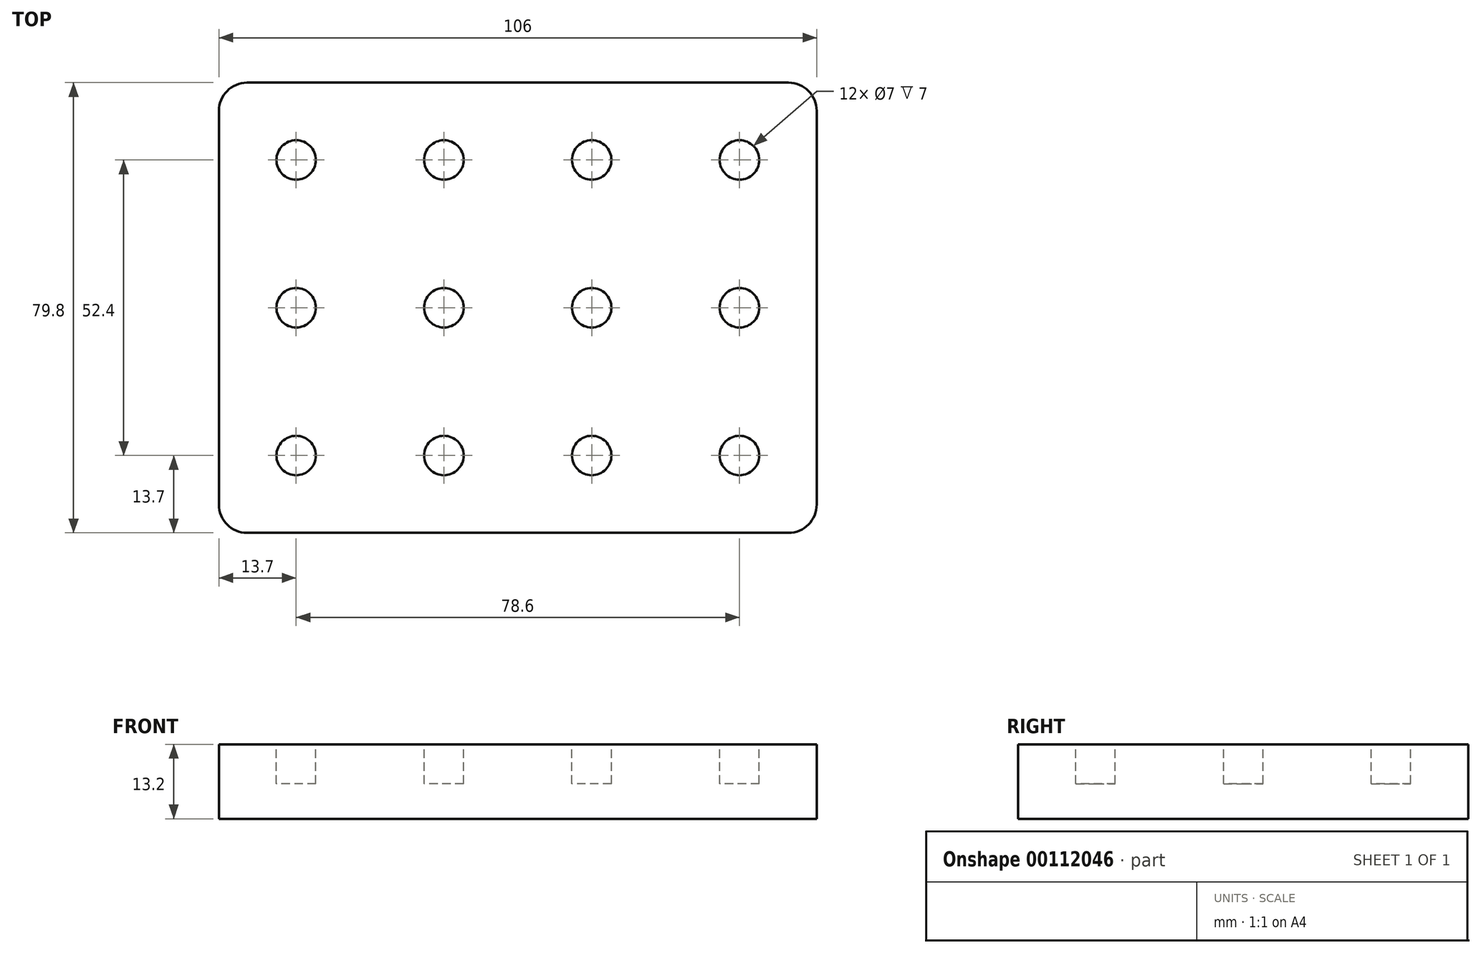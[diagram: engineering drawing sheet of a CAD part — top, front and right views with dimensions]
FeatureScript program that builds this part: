
annotation { "Feature Type Name" : "Feature", "Feature Type Description" : "" }
export const myFeature = defineFeature(function(context is Context, id is Id, definition is map)
    precondition{}
    {
        {
            var Q0;
            Q0=qCreatedBy(makeId("Top.planeOp"),FACE);
            var sketch = newSketch(context, id + "F0", { "sketchPlane" : qUnion([Q0])});
            skLineSegment(sketch, "E0.bottom", {"start": v(48, -39.9) * mm, "end": v(-48, -39.9) * mm});
            skLineSegment(sketch, "E0.top", {"start": v(48, 39.9) * mm, "end": v(-48, 39.9) * mm});
            skLineSegment(sketch, "E0.left", {"start": v(53, -34.9) * mm, "end": v(53, 34.9) * mm});
            skLineSegment(sketch, "E0.right", {"start": v(-53, -34.9) * mm, "end": v(-53, 34.9) * mm});
            skPoint(sketch, "E0.middle", {"position": v(0, 0) * mm});
            skPoint(sketch, "E1.visualSharp", {"position": v(-53, 39.9) * mm});
            skArc(sketch, "E1.filletArc", {"start": v(-48, 39.9) * mm, "mid": v(-51.54, 38.44) * mm, "end": v(-53, 34.9) * mm});
            skPoint(sketch, "E2.visualSharp", {"position": v(53, 39.9) * mm});
            skArc(sketch, "E2.filletArc", {"start": v(53, 34.9) * mm, "mid": v(51.54, 38.44) * mm, "end": v(48, 39.9) * mm});
            skPoint(sketch, "E3.visualSharp", {"position": v(53, -39.9) * mm});
            skArc(sketch, "E3.filletArc", {"start": v(48, -39.9) * mm, "mid": v(51.54, -38.44) * mm, "end": v(53, -34.9) * mm});
            skPoint(sketch, "E4.visualSharp", {"position": v(-53, -39.9) * mm});
            skArc(sketch, "E4.filletArc", {"start": v(-53, -34.9) * mm, "mid": v(-51.54, -38.44) * mm, "end": v(-48, -39.9) * mm});
            skSolve(sketch);
        }
        {
            var Q0;
            Q0=makeQuery(id+"F0.imprint","IMPRINT",FACE,{"disambiguationData":[TD([[makeQuery(id+"F0.imprint","IMPRINT",EDGE,{"derivedFrom":sQuery(id+"F0.wireOp",EDGE,"E0.bottom")}),-1.0]])]});
            var sketch = newSketch(context, id + "F1", { "sketchPlane" : qUnion([Q0])});
            skLineSegment(sketch, "E5.0", {"start": v(-51.8, -39.9) * mm, "end": v(-51.8, 39.9) * mm, "construction": true});
            skLineSegment(sketch, "E6.0", {"start": v(-51.8, -38.7) * mm, "end": v(51.8, -38.7) * mm, "construction": true});
            skLineSegment(sketch, "E6.1", {"start": v(-51.8, 38.7) * mm, "end": v(-51.8, -38.7) * mm, "construction": true});
            skLineSegment(sketch, "E6.2", {"start": v(51.8, 38.7) * mm, "end": v(-51.8, 38.7) * mm, "construction": true});
            skLineSegment(sketch, "E6.3", {"start": v(51.8, -38.7) * mm, "end": v(51.8, 38.7) * mm, "construction": true});
            skLineSegment(sketch, "E7.0", {"start": v(-26.8, 38.7) * mm, "end": v(-26.8, -38.7) * mm, "construction": true});
            skLineSegment(sketch, "E8.0", {"start": v(-25.6, 38.7) * mm, "end": v(-25.6, -38.7) * mm, "construction": true});
            skLineSegment(sketch, "E9.0", {"start": v(-0.6, 38.7) * mm, "end": v(-0.6, -38.7) * mm, "construction": true});
            skLineSegment(sketch, "E10.0", {"start": v(0.6, 38.7) * mm, "end": v(0.6, -38.7) * mm, "construction": true});
            skLineSegment(sketch, "E11.0", {"start": v(25.6, 38.7) * mm, "end": v(25.6, -38.7) * mm, "construction": true});
            skLineSegment(sketch, "E12.0", {"start": v(26.8, 38.7) * mm, "end": v(26.8, -38.7) * mm, "construction": true});
            skLineSegment(sketch, "E13.0", {"start": v(-51.8, -13.7) * mm, "end": v(51.8, -13.7) * mm, "construction": true});
            skLineSegment(sketch, "E14.0", {"start": v(-51.8, -12.5) * mm, "end": v(51.8, -12.5) * mm, "construction": true});
            skLineSegment(sketch, "E15.0", {"start": v(-51.8, 12.5) * mm, "end": v(51.8, 12.5) * mm, "construction": true});
            skLineSegment(sketch, "E16.0", {"start": v(-51.8, 13.7) * mm, "end": v(51.8, 13.7) * mm, "construction": true});
            skSolve(sketch);
        }
        {
            var Q0;
            Q0 = qSketchRegion(id + "F0", true);
            extrude(context, id + "F2", {"entities" : qUnion([Q0]), "endBound" : BoundingType.SYMMETRIC, "depth" : 13.2 * mm});
        }
        {
            var Q0;
            Q0=makeQuery(id+"F2.opExtrude","CAP_FACE",FACE,{"disambiguationData":[OSD([sQuery(id+"F0.wireOp",EDGE,"E0.bottom"),sQuery(id+"F0.wireOp",EDGE,"E0.top"),sQuery(id+"F0.wireOp",EDGE,"E0.left"),sQuery(id+"F0.wireOp",EDGE,"E0.right")])],"isStart":false});
            var sketch = newSketch(context, id + "F3", { "sketchPlane" : qUnion([Q0])});
            skCircle(sketch, "E17", {"center": v(-39.3, 26.2) * mm, "radius": 12.5 * mm});
            skCircle(sketch, "E18", {"center": v(-13.1, 26.2) * mm, "radius": 12.5 * mm});
            skCircle(sketch, "E19", {"center": v(13.1, 26.2) * mm, "radius": 12.5 * mm});
            skCircle(sketch, "E20", {"center": v(39.3, 26.2) * mm, "radius": 12.5 * mm});
            skCircle(sketch, "E21", {"center": v(39.3, 0) * mm, "radius": 12.5 * mm});
            skCircle(sketch, "E22", {"center": v(13.1, 0) * mm, "radius": 12.5 * mm});
            skCircle(sketch, "E23", {"center": v(-13.1, 0) * mm, "radius": 12.5 * mm});
            skCircle(sketch, "E24", {"center": v(-39.3, 0) * mm, "radius": 12.5 * mm});
            skCircle(sketch, "E25", {"center": v(-39.3, -26.2) * mm, "radius": 12.5 * mm});
            skCircle(sketch, "E26", {"center": v(-13.1, -26.2) * mm, "radius": 12.5 * mm});
            skCircle(sketch, "E27", {"center": v(13.1, -26.2) * mm, "radius": 12.5 * mm});
            skCircle(sketch, "E28", {"center": v(39.3, -26.2) * mm, "radius": 12.5 * mm});
            skSolve(sketch);
        }
        {
            var Q0;
            Q0=makeQuery(id+"F2.opExtrude","CAP_FACE",FACE,{"disambiguationData":[OSD([sQuery(id+"F0.wireOp",EDGE,"E0.bottom"),sQuery(id+"F0.wireOp",EDGE,"E0.top"),sQuery(id+"F0.wireOp",EDGE,"E0.left"),sQuery(id+"F0.wireOp",EDGE,"E0.right"),sQuery(id+"F0.wireOp",EDGE,"E1.filletArc"),sQuery(id+"F0.wireOp",EDGE,"E2.filletArc"),sQuery(id+"F0.wireOp",EDGE,"E3.filletArc"),sQuery(id+"F0.wireOp",EDGE,"E4.filletArc")])],"isStart":false});
            var sketch = newSketch(context, id + "F4", { "sketchPlane" : qUnion([Q0])});
            skCircle(sketch, "E29", {"center": v(-39.3, 26.2) * mm, "radius": 3.5 * mm});
            skCircle(sketch, "E30", {"center": v(-13.1, 26.2) * mm, "radius": 3.5 * mm});
            skCircle(sketch, "E31", {"center": v(13.1, 26.2) * mm, "radius": 3.5 * mm});
            skCircle(sketch, "E32", {"center": v(39.3, 26.2) * mm, "radius": 3.5 * mm});
            skCircle(sketch, "E33", {"center": v(39.3, 0) * mm, "radius": 3.5 * mm});
            skCircle(sketch, "E34", {"center": v(13.1, 0) * mm, "radius": 3.5 * mm});
            skCircle(sketch, "E35", {"center": v(-13.1, 0) * mm, "radius": 3.5 * mm});
            skCircle(sketch, "E36", {"center": v(-39.3, 0) * mm, "radius": 3.5 * mm});
            skCircle(sketch, "E37", {"center": v(-39.3, -26.2) * mm, "radius": 3.5 * mm});
            skCircle(sketch, "E38", {"center": v(-13.1, -26.2) * mm, "radius": 3.5 * mm});
            skCircle(sketch, "E39", {"center": v(13.1, -26.2) * mm, "radius": 3.5 * mm});
            skCircle(sketch, "E40", {"center": v(39.3, -26.2) * mm, "radius": 3.5 * mm});
            skSolve(sketch);
        }
        {
            var Q0;
            Q0 = qSketchRegion(id + "F4", true);
            extrude(context, id + "F5", {"entities" : qUnion([Q0]), "operationType" : NewBodyOperationType.REMOVE, "oppositeDirection" : true, "depth" : 7 * mm});
        }
    });
